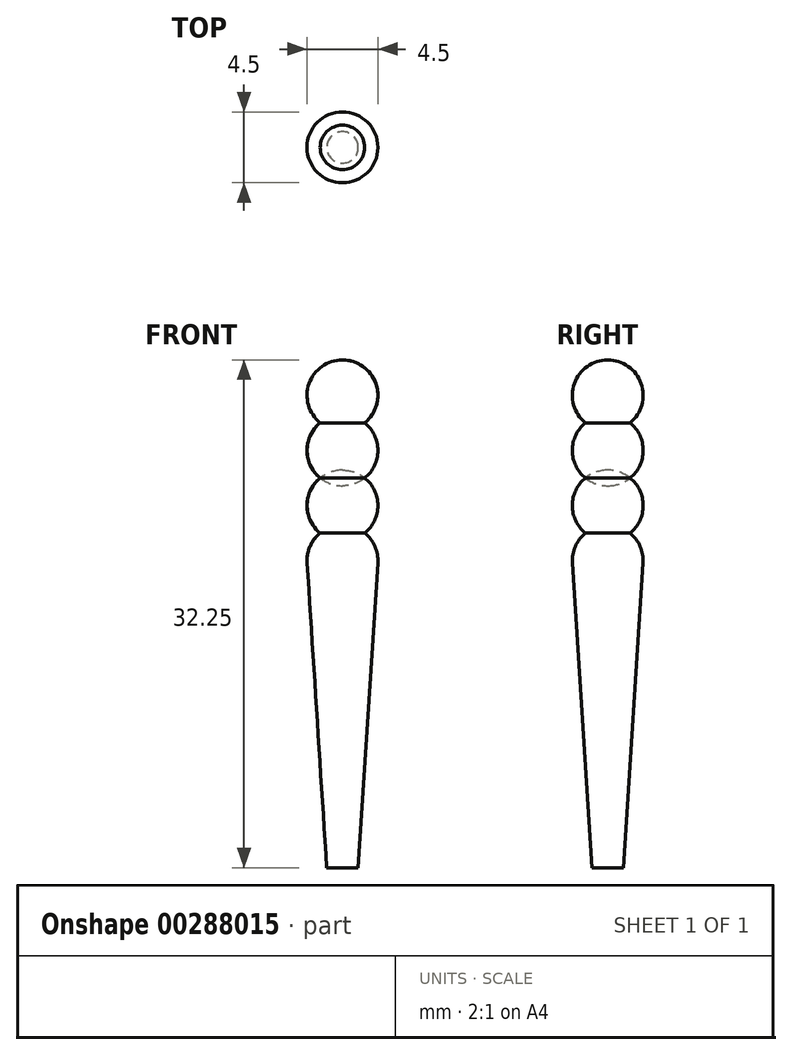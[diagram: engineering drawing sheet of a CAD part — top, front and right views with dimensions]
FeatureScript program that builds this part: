
annotation { "Feature Type Name" : "Feature", "Feature Type Description" : "" }
export const myFeature = defineFeature(function(context is Context, id is Id, definition is map)
    precondition{}
    {
        {
            var Q0;
            Q0=qCreatedBy(makeId("Front.planeOp"),FACE);
            var sketch = newSketch(context, id + "F0", { "sketchPlane" : qUnion([Q0])});
            skLineSegment(sketch, "E0", {"start": v(0, 0) * mm, "end": v(0, 30) * mm});
            skCircle(sketch, "E1", {"center": v(0, 30) * mm, "radius": 2.25 * mm});
            skCircle(sketch, "E2.1.0.0", {"center": v(0, 26.5) * mm, "radius": 2.25 * mm});
            skCircle(sketch, "E2.2.0.0", {"center": v(0, 23) * mm, "radius": 2.25 * mm});
            skCircle(sketch, "E2.3.0.0", {"center": v(0, 19.5) * mm, "radius": 2.25 * mm});
            skLineSegment(sketch, "E2.direction1", {"start": v(0, 30) * mm, "end": v(0, 26.5) * mm, "construction": true});
            skLineSegment(sketch, "E3", {"start": v(0, 0) * mm, "end": v(1, 0) * mm});
            skLineSegment(sketch, "E4", {"start": v(1, 0) * mm, "end": v(2.25, 19.36) * mm});
            skLineSegment(sketch, "E5", {"start": v(0, 30) * mm, "end": v(0, 32.25) * mm});
            skSolve(sketch);
        }
        {
            var Q0;
            {var subQ0=sQuery(id+"F0.wireOp",EDGE,"E5");Q0=makeQuery(id+"F0.imprint","IMPRINT",FACE,{"disambiguationData":[TD([[makeQuery(id+"F0.imprint","IMPRINT",EDGE,{"derivedFrom":subQ0}),-1.0]])]});}
            var Q1;
            {var subQ0=sQuery(id+"F0.wireOp",EDGE,"E1");var subQ1=sQuery(id+"F0.wireOp",EDGE,"E0");var subQ2=makeQuery(id+"F0.imprint","INTERSECT",VERTEX,{"derivedFrom":[subQ1,subQ0]});Q1=makeQuery(id+"F0.imprint","IMPRINT",FACE,{"disambiguationData":[TD([[makeQuery(id+"F0.imprint","IMPRINT",EDGE,{"disambiguationData":[TD([[subQ2,-1.0]])],"derivedFrom":subQ1}),-1.0]])]});}
            var Q2;
            {var subQ0=sQuery(id+"F0.wireOp",EDGE,"E2.2.0.0");var subQ1=sQuery(id+"F0.wireOp",EDGE,"E0");var subQ2=makeQuery(id+"F0.imprint","INTERSECT",VERTEX,{"disambiguationData":[OD(1.0)],"derivedFrom":[subQ1,subQ0]});Q2=makeQuery(id+"F0.imprint","IMPRINT",FACE,{"disambiguationData":[TD([[makeQuery(id+"F0.imprint","IMPRINT",EDGE,{"disambiguationData":[TD([[subQ2,-1.0]])],"derivedFrom":subQ1}),-1.0]])]});}
            var Q3;
            {var subQ0=sQuery(id+"F0.wireOp",EDGE,"E2.1.0.0");var subQ1=sQuery(id+"F0.wireOp",EDGE,"E0");var subQ2=makeQuery(id+"F0.imprint","INTERSECT",VERTEX,{"disambiguationData":[OD(0.0)],"derivedFrom":[subQ1,subQ0]});Q3=makeQuery(id+"F0.imprint","IMPRINT",FACE,{"disambiguationData":[TD([[makeQuery(id+"F0.imprint","IMPRINT",EDGE,{"disambiguationData":[TD([[subQ2,-1.0]])],"derivedFrom":subQ1}),-1.0]])]});}
            var Q4;
            {var subQ0=sQuery(id+"F0.wireOp",EDGE,"E2.3.0.0");var subQ1=sQuery(id+"F0.wireOp",EDGE,"E0");var subQ2=makeQuery(id+"F0.imprint","INTERSECT",VERTEX,{"disambiguationData":[OD(1.0)],"derivedFrom":[subQ1,subQ0]});Q4=makeQuery(id+"F0.imprint","IMPRINT",FACE,{"disambiguationData":[TD([[makeQuery(id+"F0.imprint","IMPRINT",EDGE,{"disambiguationData":[TD([[subQ2,-1.0]])],"derivedFrom":subQ1}),-1.0]])]});}
            var Q5;
            {var subQ0=sQuery(id+"F0.wireOp",EDGE,"E2.2.0.0");var subQ1=sQuery(id+"F0.wireOp",EDGE,"E0");var subQ2=makeQuery(id+"F0.imprint","INTERSECT",VERTEX,{"disambiguationData":[OD(0.0)],"derivedFrom":[subQ1,subQ0]});Q5=makeQuery(id+"F0.imprint","IMPRINT",FACE,{"disambiguationData":[TD([[makeQuery(id+"F0.imprint","IMPRINT",EDGE,{"disambiguationData":[TD([[subQ2,-1.0]])],"derivedFrom":subQ1}),-1.0]])]});}
            var Q6;
            {var subQ0=sQuery(id+"F0.wireOp",EDGE,"E2.3.0.0");var subQ1=sQuery(id+"F0.wireOp",EDGE,"E0");var subQ2=makeQuery(id+"F0.imprint","INTERSECT",VERTEX,{"disambiguationData":[OD(0.0)],"derivedFrom":[subQ1,subQ0]});Q6=makeQuery(id+"F0.imprint","IMPRINT",FACE,{"disambiguationData":[TD([[makeQuery(id+"F0.imprint","IMPRINT",EDGE,{"disambiguationData":[TD([[subQ2,-1.0]])],"derivedFrom":subQ1}),-1.0]])]});}
            var Q7;
            {var subQ0=sQuery(id+"F0.wireOp",EDGE,"E3");Q7=makeQuery(id+"F0.imprint","IMPRINT",FACE,{"disambiguationData":[TD([[makeQuery(id+"F0.imprint","IMPRINT",EDGE,{"derivedFrom":subQ0}),1.0]])]});}
            var Q8;
            Q8=sQuery(id+"F0.wireOp",EDGE,"E0");
            revolve(context, id + "F1", {"entities" : qUnion([Q0, Q1, Q2, Q3, Q4, Q5, Q6, Q7]), "axis" : qUnion([Q8]), "revolveType" : RevolveType.FULL});
        }
    });
